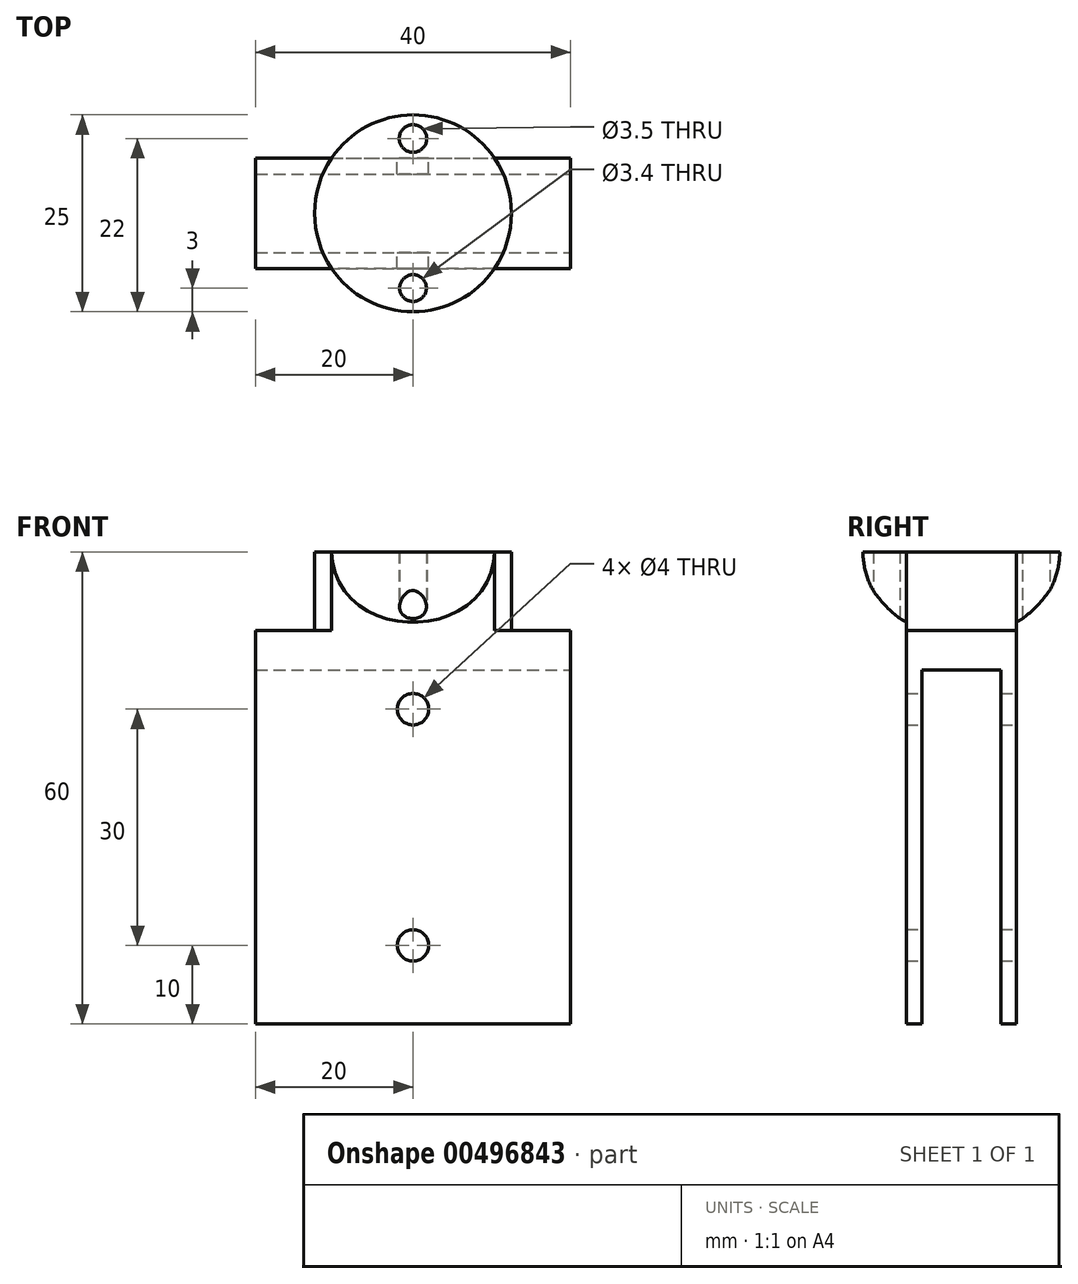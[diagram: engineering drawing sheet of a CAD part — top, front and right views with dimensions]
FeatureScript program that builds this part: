
annotation { "Feature Type Name" : "Feature", "Feature Type Description" : "" }
export const myFeature = defineFeature(function(context is Context, id is Id, definition is map)
    precondition{}
    {
        {
            var Q0;
            Q0=qCreatedBy(makeId("Front.planeOp"),FACE);
            var sketch = newSketch(context, id + "F0", { "sketchPlane" : qUnion([Q0])});
            skLineSegment(sketch, "E0.bottom", {"start": v(-20, 0) * mm, "end": v(20, 0) * mm});
            skLineSegment(sketch, "E0.top", {"start": v(-20, -50) * mm, "end": v(20, -50) * mm});
            skLineSegment(sketch, "E0.left", {"start": v(-20, 0) * mm, "end": v(-20, -50) * mm});
            skLineSegment(sketch, "E0.right", {"start": v(20, 0) * mm, "end": v(20, -50) * mm});
            skLineSegment(sketch, "E1.top", {"start": v(-20, -5) * mm, "end": v(20, -5) * mm});
            skLineSegment(sketch, "E1.left", {"start": v(-20, -50) * mm, "end": v(-20, -5) * mm});
            skLineSegment(sketch, "E1.right", {"start": v(20, -50) * mm, "end": v(20, -5) * mm});
            skLineSegment(sketch, "E2", {"start": v(0, -50) * mm, "end": v(0, -40) * mm});
            skPoint(sketch, "E2.endSnap0", {"position": v(0, -50) * mm});
            skCircle(sketch, "E3", {"center": v(0, -40) * mm, "radius": 2 * mm});
            skLineSegment(sketch, "E4", {"start": v(0, 0) * mm, "end": v(0, -10) * mm});
            skCircle(sketch, "E5", {"center": v(0, -10) * mm, "radius": 2 * mm});
            skSolve(sketch);
        }
        {
            var Q0;
            Q0=qCreatedBy(makeId("Top.planeOp"),FACE);
            var sketch = newSketch(context, id + "F1", { "sketchPlane" : qUnion([Q0])});
            skCircle(sketch, "E6", {"center": v(0, 0) * mm, "radius": 12.5 * mm});
            skLineSegment(sketch, "E7", {"start": v(0, 12.5) * mm, "end": v(0, 9.5) * mm});
            skCircle(sketch, "E8", {"center": v(0, 9.5) * mm, "radius": 1.75 * mm});
            skLineSegment(sketch, "E9", {"start": v(0, -12.5) * mm, "end": v(0, -9.5) * mm});
            skCircle(sketch, "E10", {"center": v(0, -9.5) * mm, "radius": 1.7 * mm});
            skSolve(sketch);
        }
        {
            var Q0;
            Q0=makeQuery(id+"F0.imprint","IMPRINT",FACE,{"disambiguationData":[TD([[makeQuery(id+"F0.imprint","IMPRINT",EDGE,{"derivedFrom":sQuery(id+"F0.wireOp",EDGE,"E0.bottom")}),-1.0]])]});
            var Q1;
            Q1=makeQuery(id+"F0.imprint","IMPRINT",FACE,{"disambiguationData":[TD([[makeQuery(id+"F0.imprint","IMPRINT",EDGE,{"derivedFrom":sQuery(id+"F0.wireOp",EDGE,"E0.top")}),1.0]])]});
            extrude(context, id + "F2", {"entities" : qUnion([Q0, Q1]), "depth" : 14 * mm, "symmetric" : true});
        }
        {
            var Q0;
            Q0=makeQuery(id+"F0.imprint","IMPRINT",FACE,{"disambiguationData":[TD([[makeQuery(id+"F0.imprint","IMPRINT",EDGE,{"derivedFrom":sQuery(id+"F0.wireOp",EDGE,"E0.top")}),1.0]])]});
            extrude(context, id + "F3", {"entities" : qUnion([Q0]), "operationType" : NewBodyOperationType.REMOVE, "oppositeDirection" : true, "depth" : 10 * mm, "symmetric" : true});
        }
        {
            var Q0;
            Q0=makeQuery(id+"F1.imprint","IMPRINT",FACE,{"disambiguationData":[TD([[makeQuery(id+"F1.imprint","IMPRINT",EDGE,{"derivedFrom":sQuery(id+"F1.wireOp",EDGE,"E6")}),1.0]])]});
            extrude(context, id + "F4", {"entities" : qUnion([Q0]), "operationType" : NewBodyOperationType.ADD, "depth" : 10 * mm});
        }
        {
            var Q0;
            {var subQ0=sQuery(id+"F1.wireOp",EDGE,"E6");Q0=makeQuery(id+"F4.boolean.opBoolean","SPLIT",EDGE,{"disambiguationData":[topologyDisambiguationEdgeConnected([makeQuery(id+"F2.opExtrude","SWEPT_FACE",FACE,{"disambiguationData":[OSD([sQuery(id+"F0.wireOp",EDGE,"E0.bottom")])]}),makeQuery(id+"F4.opExtrude","SWEPT_FACE",FACE,{"disambiguationData":[OSD([subQ0])]})]),OD(0.0)],"derivedFrom":makeQuery(id+"F4.opExtrude","CAP_EDGE",EDGE,{"disambiguationData":[OSD([subQ0])],"isStart":true})});}
            var Q1;
            {var subQ0=sQuery(id+"F1.wireOp",EDGE,"E6");Q1=makeQuery(id+"F4.boolean.opBoolean","SPLIT",EDGE,{"disambiguationData":[topologyDisambiguationEdgeConnected([makeQuery(id+"F2.opExtrude","SWEPT_FACE",FACE,{"disambiguationData":[OSD([sQuery(id+"F0.wireOp",EDGE,"E0.bottom")])]}),makeQuery(id+"F4.opExtrude","SWEPT_FACE",FACE,{"disambiguationData":[OSD([subQ0])]})]),OD(1.0)],"derivedFrom":makeQuery(id+"F4.opExtrude","CAP_EDGE",EDGE,{"disambiguationData":[OSD([subQ0])],"isStart":true})});}
            fillet(context, id + "F5", {"entities" : qUnion([Q0, Q1]), "radius" : 10 * mm, "tangentPropagation" : true, "allowEdgeOverflow" : false});
        }
    });
